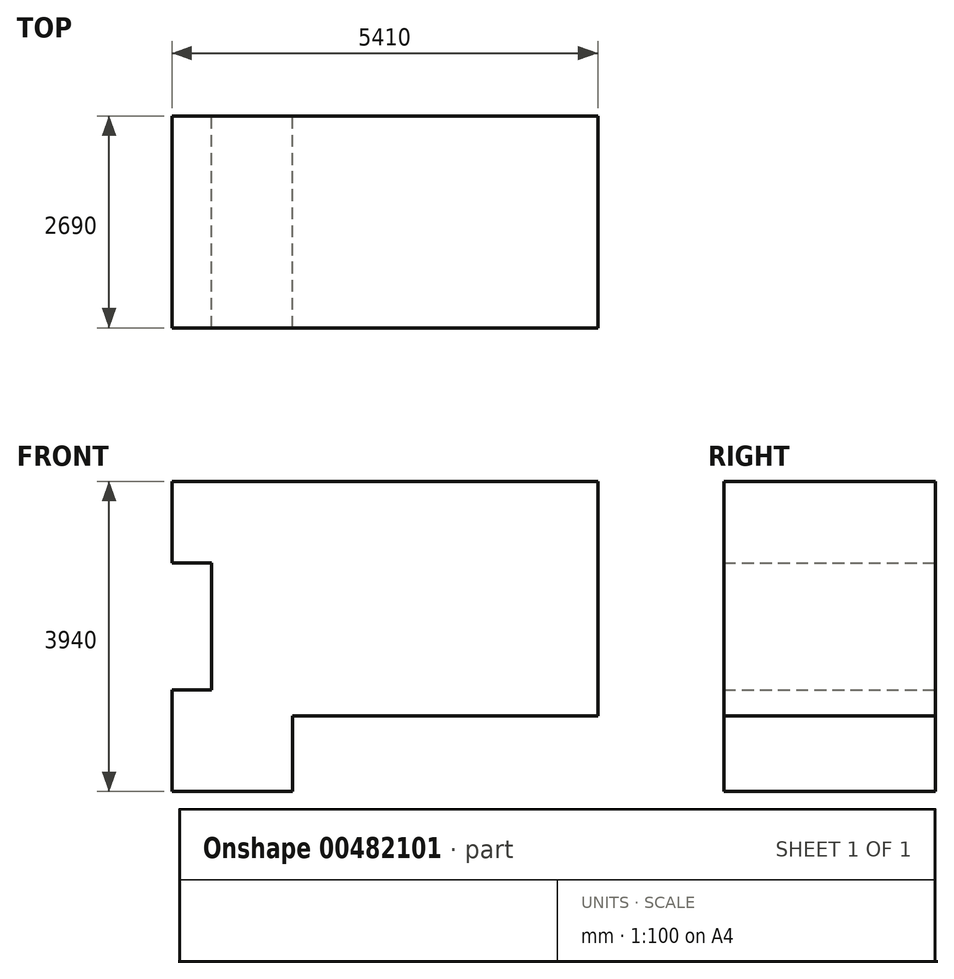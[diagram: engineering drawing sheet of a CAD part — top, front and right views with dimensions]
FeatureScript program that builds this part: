
annotation { "Feature Type Name" : "Feature", "Feature Type Description" : "" }
export const myFeature = defineFeature(function(context is Context, id is Id, definition is map)
    precondition{}
    {
        {
            var Q0;
            Q0=qCreatedBy(makeId("Front.planeOp"),FACE);
            var sketch = newSketch(context, id + "F0", { "sketchPlane" : qUnion([Q0])});
            skLineSegment(sketch, "E0", {"start": v(-2524.28, 1967.51) * mm, "end": v(2885.72, 1967.51) * mm});
            skLineSegment(sketch, "E1", {"start": v(2885.72, 1967.51) * mm, "end": v(2885.72, -1012.49) * mm});
            skLineSegment(sketch, "E2", {"start": v(2885.72, -1012.49) * mm, "end": v(-994.28, -1012.49) * mm});
            skLineSegment(sketch, "E3", {"start": v(-994.28, -1012.49) * mm, "end": v(-994.28, -1972.49) * mm});
            skLineSegment(sketch, "E4", {"start": v(-994.28, -1972.49) * mm, "end": v(-2524.28, -1972.49) * mm});
            skLineSegment(sketch, "E5", {"start": v(-2524.28, -1972.49) * mm, "end": v(-2524.28, -682.49) * mm});
            skLineSegment(sketch, "E6", {"start": v(-2524.28, -682.49) * mm, "end": v(-2024.28, -682.49) * mm});
            skLineSegment(sketch, "E7", {"start": v(-2024.28, -682.49) * mm, "end": v(-2024.28, 927.51) * mm});
            skLineSegment(sketch, "E8", {"start": v(-2024.28, 927.51) * mm, "end": v(-2524.28, 927.51) * mm});
            skLineSegment(sketch, "E9", {"start": v(-2524.28, 927.51) * mm, "end": v(-2524.28, 1967.51) * mm});
            skSolve(sketch);
        }
        {
            var Q0;
            Q0=makeQuery(id+"F0.imprint","IMPRINT",FACE,{"disambiguationData":[TD([[makeQuery(id+"F0.imprint","IMPRINT",EDGE,{"derivedFrom":sQuery(id+"F0.wireOp",EDGE,"E0")}),-1.0]])]});
            extrude(context, id + "F1", {"entities" : qUnion([Q0]), "depth" : 2690 * mm});
        }
    });
